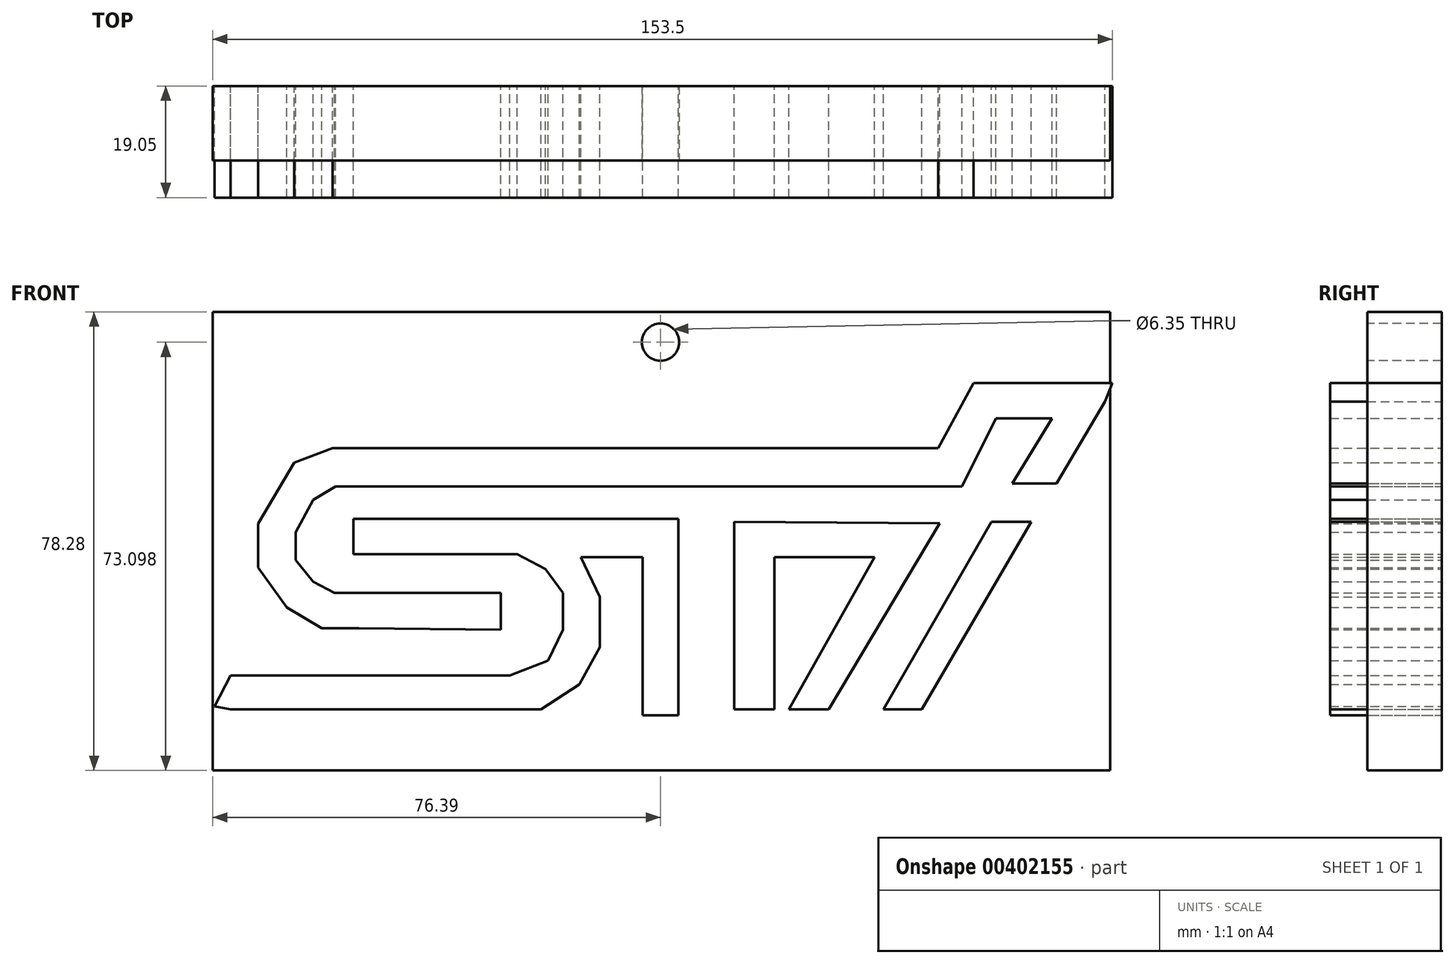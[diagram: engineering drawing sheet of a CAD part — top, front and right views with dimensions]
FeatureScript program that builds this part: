
annotation { "Feature Type Name" : "Feature", "Feature Type Description" : "" }
export const myFeature = defineFeature(function(context is Context, id is Id, definition is map)
    precondition{}
    {
        {
            var Q0;
            Q0=qCreatedBy(makeId("Front.planeOp"),FACE);
            var sketch = newSketch(context, id + "F0", { "sketchPlane" : qUnion([Q0])});
            skLineSegment(sketch, "E0", {"start": v(-76.1, -21.3) * mm, "end": v(-73.33, -16) * mm});
            skLineSegment(sketch, "E1", {"start": v(-73.33, -16) * mm, "end": v(-25.7, -16) * mm});
            skLineSegment(sketch, "E2", {"start": v(-25.7, -16) * mm, "end": v(-19.15, -13.48) * mm});
            skLineSegment(sketch, "E3", {"start": v(-19.15, -13.48) * mm, "end": v(-16.63, -8.2) * mm});
            skLineSegment(sketch, "E4", {"start": v(-25.2, -21.8) * mm, "end": v(-73.33, -21.8) * mm});
            skLineSegment(sketch, "E5", {"start": v(-73.33, -21.8) * mm, "end": v(-76.1, -21.3) * mm});
            skLineSegment(sketch, "E6", {"start": v(-16.63, -1.9) * mm, "end": v(-16.63, -8.2) * mm});
            skLineSegment(sketch, "E7", {"start": v(-13.6, 4.16) * mm, "end": v(-3.02, 4.16) * mm});
            skLineSegment(sketch, "E8", {"start": v(-3.02, 4.16) * mm, "end": v(-3.02, -22.8) * mm});
            skLineSegment(sketch, "E9", {"start": v(-3.02, -22.8) * mm, "end": v(3.02, -22.8) * mm});
            skLineSegment(sketch, "E10", {"start": v(3.02, -22.8) * mm, "end": v(3.02, 10.71) * mm});
            skLineSegment(sketch, "E11", {"start": v(3.02, 10.71) * mm, "end": v(-52.42, 10.71) * mm});
            skLineSegment(sketch, "E12", {"start": v(-52.42, 10.71) * mm, "end": v(-52.42, 4.66) * mm});
            skLineSegment(sketch, "E13", {"start": v(-52.42, 4.66) * mm, "end": v(-24.44, 4.66) * mm});
            skLineSegment(sketch, "E14", {"start": v(-24.44, 4.66) * mm, "end": v(-19.66, 2.14) * mm});
            skLineSegment(sketch, "E15", {"start": v(-19.66, 2.14) * mm, "end": v(-16.63, -1.9) * mm});
            skLineSegment(sketch, "E16", {"start": v(-27.22, -8.2) * mm, "end": v(-27.22, -1.9) * mm});
            skLineSegment(sketch, "E17", {"start": v(-27.22, -1.9) * mm, "end": v(-52.42, -1.9) * mm});
            skLineSegment(sketch, "E18", {"start": v(-52.42, -1.9) * mm, "end": v(-55.63, -1.9) * mm});
            skLineSegment(sketch, "E19", {"start": v(-55.63, -1.9) * mm, "end": v(-59.22, 0) * mm});
            skLineSegment(sketch, "E20", {"start": v(-59.22, 0) * mm, "end": v(-59.22, 3.65) * mm});
            skLineSegment(sketch, "E21", {"start": v(-25.2, -21.8) * mm, "end": v(-20.41, -21.8) * mm});
            skLineSegment(sketch, "E22", {"start": v(-20.41, -21.8) * mm, "end": v(-13.86, -17.51) * mm});
            skLineSegment(sketch, "E23", {"start": v(-13.86, -17.51) * mm, "end": v(-10.33, -11.21) * mm});
            skLineSegment(sketch, "E24", {"start": v(-10.33, -11.21) * mm, "end": v(-10.33, -2.65) * mm});
            skLineSegment(sketch, "E25", {"start": v(-10.33, -2.65) * mm, "end": v(-13.6, 4.16) * mm});
            skLineSegment(sketch, "E26", {"start": v(12.6, 10.2) * mm, "end": v(12.6, -21.8) * mm});
            skLineSegment(sketch, "E27", {"start": v(12.6, -21.8) * mm, "end": v(19.4, -21.8) * mm});
            skLineSegment(sketch, "E28", {"start": v(19.4, -21.8) * mm, "end": v(19.4, 4.16) * mm});
            skLineSegment(sketch, "E29", {"start": v(19.4, 4.16) * mm, "end": v(36.54, 4.16) * mm});
            skLineSegment(sketch, "E30", {"start": v(36.54, 4.16) * mm, "end": v(21.92, -21.8) * mm});
            skLineSegment(sketch, "E31", {"start": v(21.92, -21.8) * mm, "end": v(28.73, -21.8) * mm});
            skLineSegment(sketch, "E32", {"start": v(28.73, -21.8) * mm, "end": v(47.63, 9.95) * mm});
            skLineSegment(sketch, "E33", {"start": v(47.63, 9.95) * mm, "end": v(12.6, 10.2) * mm});
            skLineSegment(sketch, "E34", {"start": v(56.45, 10.2) * mm, "end": v(63.25, 10.2) * mm});
            skLineSegment(sketch, "E35", {"start": v(63.25, 10.2) * mm, "end": v(44.6, -21.8) * mm});
            skLineSegment(sketch, "E36", {"start": v(44.6, -21.8) * mm, "end": v(38.05, -21.8) * mm});
            skLineSegment(sketch, "E37", {"start": v(38.05, -21.8) * mm, "end": v(56.45, 10.2) * mm});
            skLineSegment(sketch, "E38", {"start": v(59.98, 16.76) * mm, "end": v(67.54, 16.76) * mm});
            skLineSegment(sketch, "E39", {"start": v(67.54, 16.76) * mm, "end": v(77.11, 32.9) * mm});
            skLineSegment(sketch, "E40", {"start": v(51.4, 16.26) * mm, "end": v(57.2, 27.86) * mm});
            skLineSegment(sketch, "E41", {"start": v(57.2, 27.86) * mm, "end": v(66.78, 27.86) * mm});
            skLineSegment(sketch, "E42", {"start": v(66.78, 27.86) * mm, "end": v(59.98, 16.76) * mm});
            skLineSegment(sketch, "E43", {"start": v(53.42, 33.91) * mm, "end": v(77.11, 33.91) * mm});
            skLineSegment(sketch, "E44", {"start": v(53.42, 33.91) * mm, "end": v(47.37, 22.81) * mm});
            skLineSegment(sketch, "E45", {"start": v(47.37, 22.81) * mm, "end": v(-55.96, 22.81) * mm});
            skLineSegment(sketch, "E46", {"start": v(-55.96, 22.81) * mm, "end": v(-62.51, 20.3) * mm});
            skLineSegment(sketch, "E47", {"start": v(-62.51, 20.3) * mm, "end": v(-64.71, 16.58) * mm});
            skLineSegment(sketch, "E48", {"start": v(-64.71, 16.58) * mm, "end": v(-68.67, 9.91) * mm});
            skLineSegment(sketch, "E49", {"start": v(-68.67, 9.91) * mm, "end": v(-68.67, 2.39) * mm});
            skLineSegment(sketch, "E50", {"start": v(-68.67, 2.39) * mm, "end": v(-63.78, -4.42) * mm});
            skLineSegment(sketch, "E51", {"start": v(-63.78, -4.42) * mm, "end": v(-57.8, -7.97) * mm});
            skLineSegment(sketch, "E52", {"start": v(-57.8, -7.97) * mm, "end": v(-51.44, -7.97) * mm});
            skLineSegment(sketch, "E53", {"start": v(-51.44, -7.97) * mm, "end": v(-27.22, -8.2) * mm});
            skLineSegment(sketch, "E54", {"start": v(51.4, 16.26) * mm, "end": v(-51.17, 16.26) * mm});
            skLineSegment(sketch, "E55", {"start": v(-51.17, 16.26) * mm, "end": v(-55.46, 16.26) * mm});
            skLineSegment(sketch, "E56", {"start": v(-55.46, 16.26) * mm, "end": v(-59.22, 13.99) * mm});
            skLineSegment(sketch, "E57", {"start": v(-59.22, 13.99) * mm, "end": v(-62.26, 8.44) * mm});
            skLineSegment(sketch, "E58", {"start": v(-62.26, 8.44) * mm, "end": v(-62.26, 3.65) * mm});
            skLineSegment(sketch, "E59", {"start": v(-62.26, 3.65) * mm, "end": v(-59.22, 0) * mm});
            skLineSegment(sketch, "E60", {"start": v(77.11, 33.91) * mm, "end": v(75.82, 30.72) * mm});
            skSolve(sketch);
        }
        {
            var Q0;
            Q0=makeQuery(id+"F0.imprint","IMPRINT",FACE,{"disambiguationData":[TD([[makeQuery(id+"F0.imprint","IMPRINT",EDGE,{"derivedFrom":sQuery(id+"F0.wireOp",EDGE,"E34")}),-1.0]])]});
            var Q1;
            Q1=makeQuery(id+"F0.imprint","IMPRINT",FACE,{"disambiguationData":[TD([[makeQuery(id+"F0.imprint","IMPRINT",EDGE,{"derivedFrom":sQuery(id+"F0.wireOp",EDGE,"E26")}),1.0]])]});
            var Q2;
            Q2=makeQuery(id+"F0.imprint","IMPRINT",FACE,{"disambiguationData":[TD([[makeQuery(id+"F0.imprint","IMPRINT",EDGE,{"derivedFrom":sQuery(id+"F0.wireOp",EDGE,"E16")}),1.0]])]});
            var Q3;
            Q3=makeQuery(id+"F0.imprint","IMPRINT",FACE,{"disambiguationData":[TD([[makeQuery(id+"F0.imprint","IMPRINT",EDGE,{"derivedFrom":sQuery(id+"F0.wireOp",EDGE,"E0")}),-1.0]])]});
            extrude(context, id + "F1", {"entities" : qUnion([Q0, Q1, Q2, Q3]), "depth" : 19.05 * mm});
        }
        {
            var Q0;
            Q0=qCreatedBy(makeId("Front.planeOp"),FACE);
            var sketch = newSketch(context, id + "F2", { "sketchPlane" : qUnion([Q0])});
            skLineSegment(sketch, "E61.bottom", {"start": v(76.72, 46.05) * mm, "end": v(-76.39, 46.05) * mm});
            skLineSegment(sketch, "E61.top", {"start": v(76.72, -32.23) * mm, "end": v(-76.39, -32.23) * mm});
            skLineSegment(sketch, "E61.left", {"start": v(76.72, 46.05) * mm, "end": v(76.72, -32.23) * mm});
            skLineSegment(sketch, "E61.right", {"start": v(-76.39, 46.05) * mm, "end": v(-76.39, -32.23) * mm});
            skSolve(sketch);
        }
        {
            var Q0;
            Q0=makeQuery(id+"F2.imprint","IMPRINT",FACE,{"disambiguationData":[TD([[makeQuery(id+"F2.imprint","IMPRINT",EDGE,{"derivedFrom":sQuery(id+"F2.wireOp",EDGE,"E61.bottom")}),1.0]])]});
            extrude(context, id + "F3", {"entities" : qUnion([Q0]), "depth" : 12.7 * mm});
        }
        {
            var Q0;
            Q0=makeQuery(id+"F3.opExtrude","CAP_FACE",FACE,{"disambiguationData":[OSD([sQuery(id+"F2.wireOp",EDGE,"E61.bottom"),sQuery(id+"F2.wireOp",EDGE,"E61.top"),sQuery(id+"F2.wireOp",EDGE,"E61.left"),sQuery(id+"F2.wireOp",EDGE,"E61.right")])],"isStart":false});
            var sketch = newSketch(context, id + "F4", { "sketchPlane" : qUnion([Q0])});
            skCircle(sketch, "E62", {"center": v(0, 40.87) * mm, "radius": 3.72 * mm});
            skSolve(sketch);
        }
        {
            var Q0;
            Q0=sQuery(id+"F4.wireOp",VERTEX,"E62.center");
            var Q1;
            Q1=makeQuery(id+"F3.opExtrude","SWEPT_BODY",BODY,{"disambiguationData":[OSD([sQuery(id+"F2.wireOp",EDGE,"E61.bottom"),sQuery(id+"F2.wireOp",EDGE,"E61.top"),sQuery(id+"F2.wireOp",EDGE,"E61.left"),sQuery(id+"F2.wireOp",EDGE,"E61.right")])]});
            hole(context, id + "F5", {"style" : HoleStyle.SIMPLE, "endStyle" : HoleEndStyle.THROUGH, "holeDiameter" : 6.35 * mm, "isTappedThrough" : true, "tappedDepth" : 12.7 * mm, "tapClearance" : 3, "locations" : qUnion([Q0]), "scope" : qUnion([Q1])});
        }
    });
